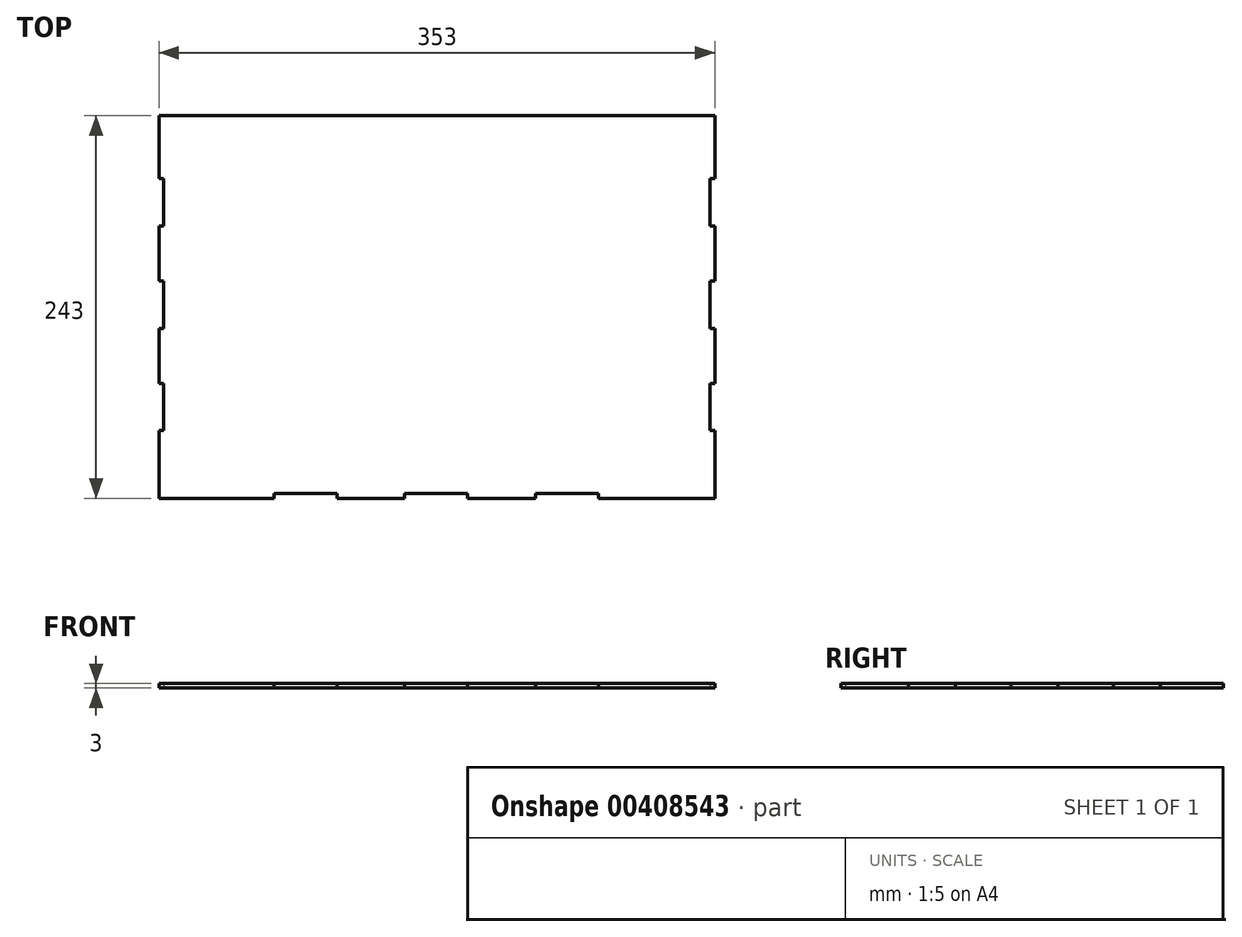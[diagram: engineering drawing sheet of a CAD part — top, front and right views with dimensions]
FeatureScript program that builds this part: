
annotation { "Feature Type Name" : "Feature", "Feature Type Description" : "" }
export const myFeature = defineFeature(function(context is Context, id is Id, definition is map)
    precondition{}
    {
        {
            var Q0;
            Q0=qCreatedBy(makeId("Top.planeOp"),FACE);
            var sketch = newSketch(context, id + "F0", { "sketchPlane" : qUnion([Q0])});
            skLineSegment(sketch, "E0", {"start": v(-188.81, 0) * mm, "end": v(-188.81, 43) * mm});
            skLineSegment(sketch, "E1", {"start": v(-188.81, 243) * mm, "end": v(164.19, 243) * mm});
            skLineSegment(sketch, "E2", {"start": v(164.19, 243) * mm, "end": v(164.19, 203) * mm});
            skLineSegment(sketch, "E3", {"start": v(164.19, 0) * mm, "end": v(90.19, 0) * mm});
            skLineSegment(sketch, "E4", {"start": v(90.19, 0) * mm, "end": v(90.19, 3) * mm});
            skLineSegment(sketch, "E5", {"start": v(90.19, 3) * mm, "end": v(50.19, 3) * mm});
            skLineSegment(sketch, "E6", {"start": v(50.19, 3) * mm, "end": v(50.19, 0) * mm});
            skLineSegment(sketch, "E7", {"start": v(50.19, 0) * mm, "end": v(7.19, 0) * mm});
            skLineSegment(sketch, "E8", {"start": v(7.19, 0) * mm, "end": v(7.19, 3) * mm});
            skLineSegment(sketch, "E9", {"start": v(7.19, 3) * mm, "end": v(-32.81, 3) * mm});
            skLineSegment(sketch, "E10", {"start": v(-32.81, 3) * mm, "end": v(-32.81, 0) * mm});
            skLineSegment(sketch, "E11", {"start": v(-32.81, 0) * mm, "end": v(-75.81, 0) * mm});
            skLineSegment(sketch, "E12", {"start": v(-75.81, 0) * mm, "end": v(-75.81, 3) * mm});
            skLineSegment(sketch, "E13", {"start": v(-75.81, 3) * mm, "end": v(-115.81, 3) * mm});
            skLineSegment(sketch, "E14", {"start": v(-115.81, 3) * mm, "end": v(-115.81, 0) * mm});
            skLineSegment(sketch, "E15.trimOffspring", {"start": v(-115.81, 0) * mm, "end": v(-188.81, 0) * mm});
            skLineSegment(sketch, "E16", {"start": v(164.19, 43) * mm, "end": v(161.19, 43) * mm});
            skLineSegment(sketch, "E17", {"start": v(161.19, 43) * mm, "end": v(161.19, 73) * mm});
            skLineSegment(sketch, "E18", {"start": v(161.19, 73) * mm, "end": v(164.19, 73) * mm});
            skLineSegment(sketch, "E19", {"start": v(164.19, 73) * mm, "end": v(164.19, 108) * mm});
            skLineSegment(sketch, "E20", {"start": v(164.19, 108) * mm, "end": v(161.19, 108) * mm});
            skLineSegment(sketch, "E21", {"start": v(161.19, 108) * mm, "end": v(161.19, 138) * mm});
            skLineSegment(sketch, "E22", {"start": v(161.19, 138) * mm, "end": v(164.19, 138) * mm});
            skLineSegment(sketch, "E23", {"start": v(164.19, 138) * mm, "end": v(164.19, 173) * mm});
            skLineSegment(sketch, "E24", {"start": v(164.19, 173) * mm, "end": v(161.19, 173) * mm});
            skLineSegment(sketch, "E25", {"start": v(161.19, 173) * mm, "end": v(161.19, 203) * mm});
            skLineSegment(sketch, "E26", {"start": v(161.19, 203) * mm, "end": v(164.19, 203) * mm});
            skLineSegment(sketch, "E27", {"start": v(-188.81, 43) * mm, "end": v(-185.81, 43) * mm});
            skLineSegment(sketch, "E28", {"start": v(-185.81, 43) * mm, "end": v(-185.81, 73) * mm});
            skLineSegment(sketch, "E29", {"start": v(-185.81, 73) * mm, "end": v(-188.81, 73) * mm});
            skLineSegment(sketch, "E30", {"start": v(-188.81, 73) * mm, "end": v(-188.81, 108) * mm});
            skLineSegment(sketch, "E31", {"start": v(-188.81, 108) * mm, "end": v(-185.81, 108) * mm});
            skLineSegment(sketch, "E32", {"start": v(-185.81, 108) * mm, "end": v(-185.81, 138) * mm});
            skLineSegment(sketch, "E33", {"start": v(-185.81, 138) * mm, "end": v(-188.81, 138) * mm});
            skLineSegment(sketch, "E34", {"start": v(-188.81, 138) * mm, "end": v(-188.81, 173) * mm});
            skLineSegment(sketch, "E35", {"start": v(-188.81, 173) * mm, "end": v(-185.81, 173) * mm});
            skLineSegment(sketch, "E36", {"start": v(-185.81, 173) * mm, "end": v(-185.81, 203) * mm});
            skLineSegment(sketch, "E37", {"start": v(-185.81, 203) * mm, "end": v(-188.81, 203) * mm});
            skLineSegment(sketch, "E38.trimOffspring", {"start": v(-188.81, 203) * mm, "end": v(-188.81, 243) * mm});
            skLineSegment(sketch, "E39.trimOffspring", {"start": v(164.19, 173) * mm, "end": v(164.19, 138) * mm});
            skLineSegment(sketch, "E40.trimOffspring", {"start": v(164.19, 108) * mm, "end": v(164.19, 73) * mm});
            skLineSegment(sketch, "E41.trimOffspring", {"start": v(164.19, 43) * mm, "end": v(164.19, 0) * mm});
            skSolve(sketch);
        }
        {
            var Q0;
            Q0=makeQuery(id+"F0.imprint","IMPRINT",FACE,{"disambiguationData":[TD([[makeQuery(id+"F0.imprint","IMPRINT",EDGE,{"derivedFrom":sQuery(id+"F0.wireOp",EDGE,"E0")}),-1.0]])]});
            extrude(context, id + "F1", {"entities" : qUnion([Q0]), "depth" : 3 * mm});
        }
    });
